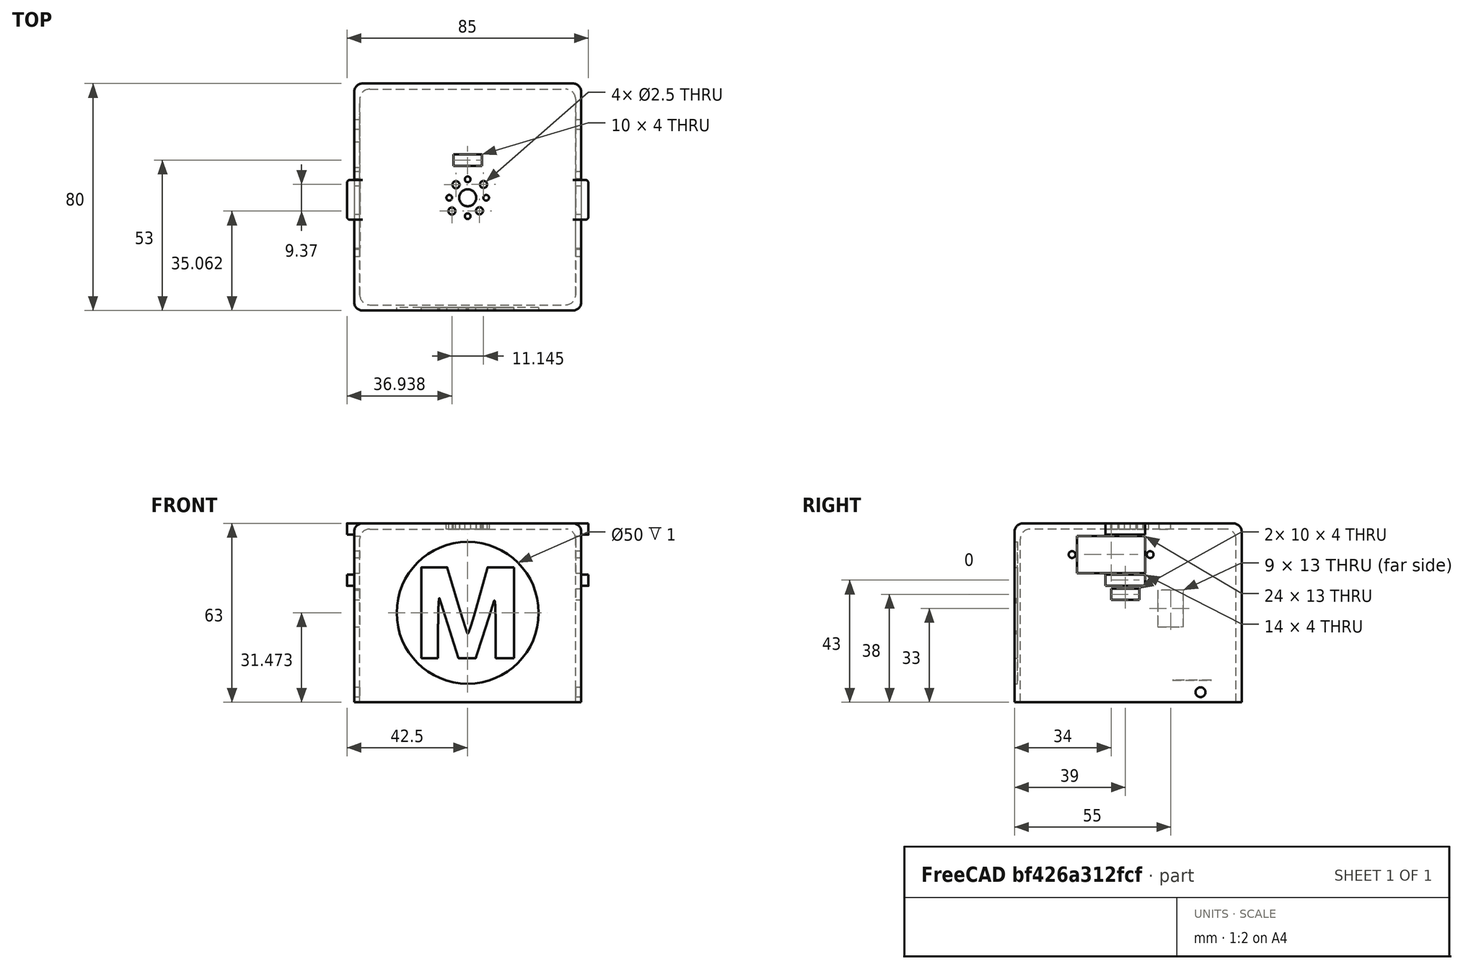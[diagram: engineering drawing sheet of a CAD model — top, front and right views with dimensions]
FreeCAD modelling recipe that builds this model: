
FCSTD DOCUMENT  (FreeCAD 0.16R6712 (Git))
Label: body_make
License: All rights reserved
LicenseURL: http://en.wikipedia.org/wiki/All_rights_reserved
objects: Part::Feature×7, Sketcher::SketchObject×2, PartDesign::Pad×2, Part::Extrusion×2, Part::Cut×2, Mesh::Feature×1, Part::MultiCommon×1, Part::Fillet×1
note: 19 computed .brp shape members not serialized (recipe doc carries the construction recipe); baked Part::Feature solids carry a one-line shape summary decoded from their .brp

FEATURE [Mesh::Feature] Robot_Front
FEATURE [Part::Feature] Part__Feature  label="body_more_holes_nano_sensor_shield"
  shape: bbox 85 x 80 x 63 mm, 96 faces (baked)
FEATURE [Part::Feature] Robot_Front001
  shape: bbox 121.9 x 121.5 x 90.22 mm, 8846 faces, 0 solids (baked)
FEATURE [Part::Feature] Robot_Front001001  label="Robot_Front002"
  shape: bbox 121.9 x 121.5 x 90.22 mm, 7163 faces, 0 solids (baked)
FEATURE [Part::Feature] Robot_Front001001_solid  label="Robot_Front002 (Solid)"
  shape: bbox 121.9 x 121.5 x 90.22 mm, 7163 faces (baked)
FEATURE [Sketcher::SketchObject] Sketch
  Placement = pos=(0,-57,0) rot=(1,0,0;1.5708rad)
  sketch-geometry (1):
    g0: Circle CenterX=0 CenterY=132.828 CenterZ=0 NormalX=0 NormalY=0 NormalZ=1 Radius=33.9464
  constraints (1):
    c: PointOnObject(g0,g-2)
FEATURE [PartDesign::Pad] Pad
  Length = 5
  Length2 = 100
  Placement = pos=(0,-57,0) rot=(1,0,0;1.5708rad)
  Reversed = true
  Sketch = -> Sketch
  Type = 0
FEATURE [Part::MultiCommon] Common
  Shapes = -> [Robot_Front001001_solid,Pad]
FEATURE [Part::Feature] Robot_Front001001_solid001  label="Robot_Front002 (Solid)001"
  shape: bbox 121.9 x 121.5 x 90.22 mm, 7163 faces (baked)
FEATURE [Part::Feature] path3506
  shape: bbox 49.46 x 49.13 x 2e-07 mm, 0 faces, 0 solids (baked)
FEATURE [Part::Feature] path3506001
  Placement = pos=(0,0,10) rot=(0,0,1;0rad)
  shape: bbox 32.55 x 31.98 x 2e-07 mm, 0 faces, 0 solids (baked)
FEATURE [Part::Extrusion] Extrude
  Base = -> path3506
  Dir = (0,0,10)
  Solid = true
FEATURE [Part::Extrusion] Extrude001
  Base = -> path3506001
  Dir = (0,0,-20)
  Solid = true
FEATURE [Sketcher::SketchObject] Sketch001
  sketch-geometry (1):
    g0: Circle CenterX=25 CenterY=-5.32684 CenterZ=0 NormalX=0 NormalY=0 NormalZ=1 Radius=25
  constraints (1):
    c: Radius(g0) = 25
FEATURE [PartDesign::Pad] Pad001
  Length = 10
  Length2 = 100
  Sketch = -> Sketch001
  Type = 0
FEATURE [Part::Cut] Cut  label="make_logo"
  Base = -> Pad001
  Placement = pos=(-264,14,106.8) rot=(1,0,0;1.5708rad)
  Tool = -> Extrude001
FEATURE [Part::Cut] Cut001  label="make_robot_body"
  Base = -> Part__Feature
  Tool = -> Cut
FEATURE [Part::Fillet] Fillet  label="body_make_bot_rounded"
  Base = -> Cut001
  Edges = 4 edges r=3: [Edge1,Edge5,Edge11,Edge15]
